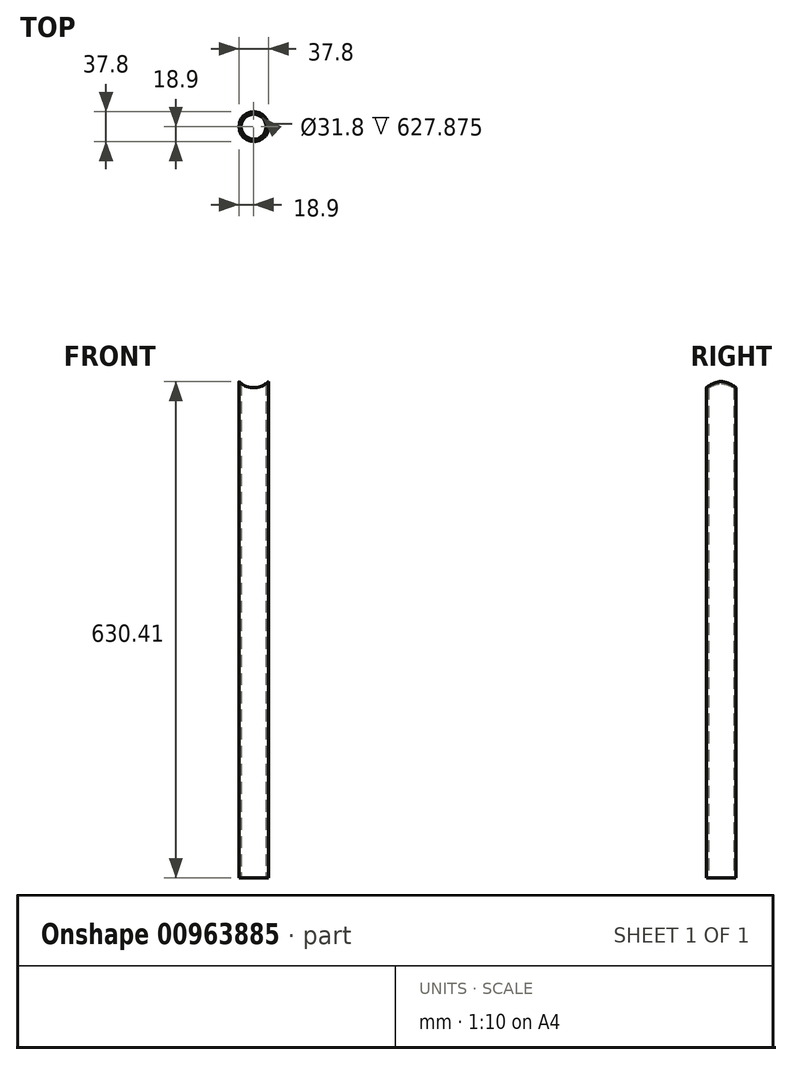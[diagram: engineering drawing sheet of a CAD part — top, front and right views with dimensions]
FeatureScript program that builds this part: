
annotation { "Feature Type Name" : "Feature", "Feature Type Description" : "" }
export const myFeature = defineFeature(function(context is Context, id is Id, definition is map)
    precondition{}
    {
        {
            var Q0;
            Q0=qCreatedBy(makeId("Top.planeOp"),FACE);
            var sketch = newSketch(context, id + "F0", { "sketchPlane" : qUnion([Q0])});
            skCircle(sketch, "E0", {"center": v(0, 0) * mm, "radius": 15.9 * mm});
            skCircle(sketch, "E1", {"center": v(0, 0) * mm, "radius": 18.9 * mm});
            skSolve(sketch);
        }
        {
            var Q0;
            Q0=makeQuery(id+"F0.imprint","IMPRINT",FACE,{"disambiguationData":[TD([[makeQuery(id+"F0.imprint","IMPRINT",EDGE,{"derivedFrom":sQuery(id+"F0.wireOp",EDGE,"E0")}),-1.0]])]});
            extrude(context, id + "F1", {"entities" : qUnion([Q0]), "depth" : 649.7 * mm, "offsetDistance" : 25 * mm});
        }
        {
            var Q0;
            Q0=qCreatedBy(makeId("Front.planeOp"),FACE);
            var sketch = newSketch(context, id + "F2", { "sketchPlane" : qUnion([Q0])});
            skLineSegment(sketch, "E2", {"start": v(0, 0) * mm, "end": v(0, 794.75) * mm, "construction": true});
            skSolve(sketch);
        }
        {
            var Q0;
            Q0=makeQuery(id+"F1.opExtrude","CAP_FACE",FACE,{"disambiguationData":[OSD([sQuery(id+"F0.wireOp",EDGE,"E0"),sQuery(id+"F0.wireOp",EDGE,"E1")])],"isStart":false});
            var sketch = newSketch(context, id + "F3", { "sketchPlane" : qUnion([Q0])});
            skLineSegment(sketch, "E3", {"start": v(0, -41.78) * mm, "end": v(0, 40.35) * mm, "construction": true});
            skLineSegment(sketch, "E4", {"start": v(-49.62, 0) * mm, "end": v(46.23, 0) * mm, "construction": true});
            skSolve(sketch);
        }
        {
            var Q0;
            Q0=sQuery(id+"F3.wireOp",EDGE,"E4");
            var Q1;
            Q1=sQuery(id+"F3.wireOp",EDGE,"E3");
            cPlane(context, id + "F4", {"entities" : qUnion([Q0, Q1]), "cplaneType" : CPlaneType.LINE_ANGLE, "offset" : 25 * mm, "angle" : 90 * degree, "width" : 150 * mm, "height" : 150 * mm});
        }
        {
            var Q0;
            Q0=qCreatedBy(id+"F4.planeOp",FACE);
            var sketch = newSketch(context, id + "F5", { "sketchPlane" : qUnion([Q0])});
            skCircle(sketch, "E5", {"center": v(0, 649.7) * mm, "radius": 27 * mm});
            skSolve(sketch);
        }
        {
            var Q0;
            Q0=makeQuery(id+"F5.imprint","IMPRINT",FACE,{"disambiguationData":[TD([[makeQuery(id+"F5.imprint","IMPRINT",EDGE,{"derivedFrom":sQuery(id+"F5.wireOp",EDGE,"E5")}),1.0]])]});
            extrude(context, id + "F6", {"entities" : qUnion([Q0]), "operationType" : NewBodyOperationType.REMOVE, "endBound" : BoundingType.SYMMETRIC, "oppositeDirection" : true, "depth" : 100 * mm, "offsetDistance" : 25 * mm});
        }
    });
